# Revit family: Vitocell 300 EVBB 119
name_source: partatom
category: Mechanical Equipment
units: mm (PartAtom-declared; Revit-internal decimal feet)

## family parameters
Always vertical = Yes
Classification = None
Cut with Voids When Loaded = No
OmniClass Number = 23.65.35.11.11
OmniClass Title = Storage Water Heaters
Part Type = Normal
Room Calculation Point = No
Round Connector Dimension = Use Diameter
Shared = No
Work Plane-Based = No

## types (1)
- Standard
    Connector_10_Diameter = 0' - 1"
    Connector_11_Diameter = 0' - 1"
    Connector_12_Diameter = 0' - 1 1/4"
    Connector_7_Diameter = 0' - 1 1/4"
    Connector_8_Diameter = 0' - 1"
    Connector_9_Diameter = 0' - 1"
    Default Elevation = 0' - 0"
    Description = Indirect Fired Domestic Hot Water Storage Tank
    Manufacturer = Viessmann
    Model = Vitocell 300 EVBB - 119 Gallons
    URL = www.viessmann.com

## geometry (parser evidence)
native form markers: Sweep x3
no freeform markers — native parametric forms only
